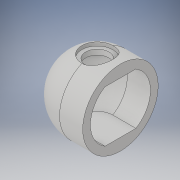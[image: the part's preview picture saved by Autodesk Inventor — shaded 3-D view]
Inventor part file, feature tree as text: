
AUTODESK INVENTOR PART (.ipt)
format: ipt  version: 2017 (Build 210142000, 142)  size: 185,344 bytes
history: native  units: in
note: dims shown in document units (in); Inventor stores cm internally (conversion verified against a paired STEP export)
features: sketch x4, extrude x2, other x1, sweep x1, plane x1
ambient origin geometry x8: Origin, YZ Plane, XZ Plane, XY Plane, X Axis, Y Axis, Z Axis, Center Point
bodies: Solid1 (feature_tree)
feature tree (9):
  other  "way up"
  extrude  "corridor"  Depth=1.0in
  sweep  "end dome"
  plane  "Work Plane1"
  extrude  "connection for pipe"  Depth=2.0in TaperAngle=0.0deg
  sketch  "Sketch1"  dims[d0=6.6667in d1=4.0in d2=2.0in d3=0.0in d6=1.0in]
  sketch  "Sketch2"  dims[d7=1.0in d8=0.0in d9=0.0in]
  sketch  "Sketch3"  dims[d10=3.0in d11=2.0in d12=0.0in]
  sketch  "Sketch5"  dims[d13=5.0in d14=4.0in d15=1.0in d16=0.0in]
